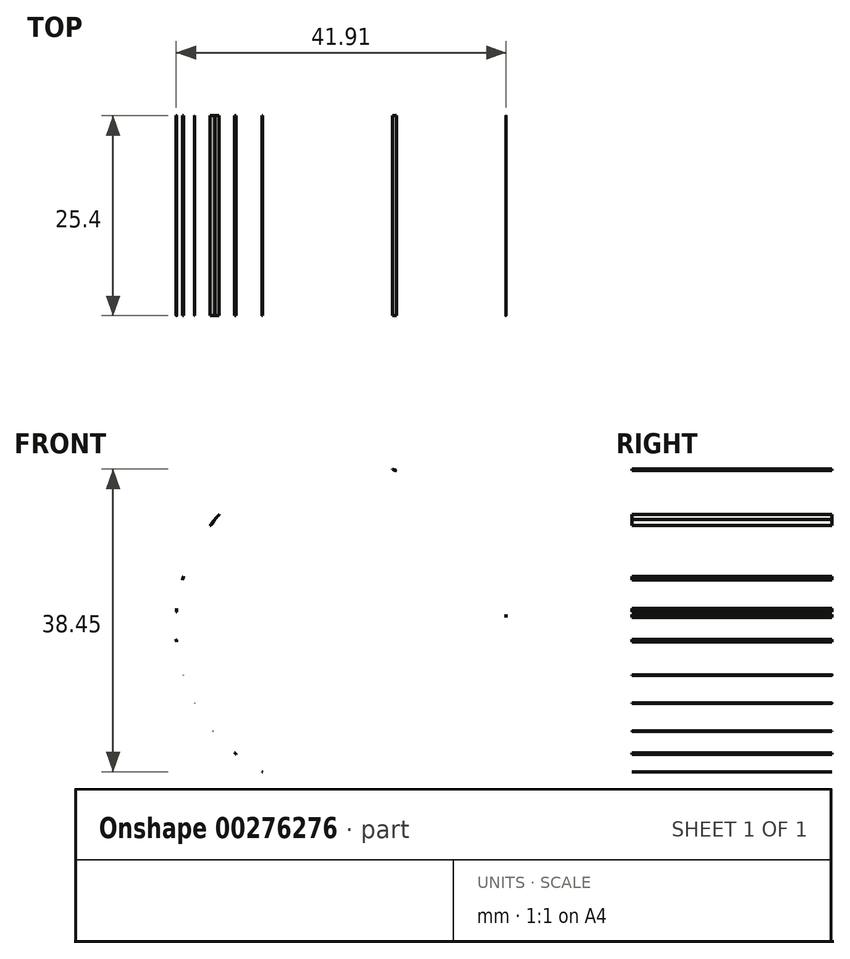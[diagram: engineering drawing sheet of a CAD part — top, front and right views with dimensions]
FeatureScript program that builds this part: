
annotation { "Feature Type Name" : "Feature", "Feature Type Description" : "" }
export const myFeature = defineFeature(function(context is Context, id is Id, definition is map)
    precondition{}
    {
        {
            var Q0;
            Q0=qCreatedBy(makeId("Front.planeOp"),FACE);
            var sketch = newSketch(context, id + "F0", { "sketchPlane" : qUnion([Q0])});
            skArc(sketch, "E0", {"start": v(-8.8, 19.07) * mm, "mid": v(-9.64, 18.66) * mm, "end": v(-10.46, 18.21) * mm});
            skFitSpline(sketch, "E1", {"points": [v(-18.48, 9.99) * mm, v(-18.56, 11.27) * mm, v(-19.16, 12.08) * mm, v(-19.57, 12.7) * mm, v(-19.03, 13.5) * mm, v(-18.35, 13.3) * mm, v(-16.64, 12.82) * mm, v(-16.01, 13.59) * mm, v(-15.5, 14.18) * mm], "startDerivative": vector(0.44, 9.8) * mm, "endDerivative": vector(5.2, 4.49) * mm});
            skFitSpline(sketch, "E2", {"points": [v(-15.5, 14.18) * mm, v(-15.5, 14.85) * mm, v(-16.13, 15.84) * mm, v(-16.63, 16.6) * mm, v(-16.17, 16.83) * mm, v(-15.5, 16.43) * mm, v(-13.9, 15.74) * mm], "startDerivative": vector(0.69, 4.6) * mm, "endDerivative": vector(7.86, -2.86) * mm});
            skFitSpline(sketch, "E3", {"points": [v(-12.52, 16.87) * mm, v(-12.57, 17.55) * mm, v(-12.93, 18.36) * mm, v(-13.16, 19.22) * mm, v(-12.39, 19.76) * mm, v(-11.67, 19.27) * mm, v(-10.46, 18.21) * mm], "startDerivative": vector(-0.05, 4.91) * mm, "endDerivative": vector(6.08, -4.97) * mm});
            skFitSpline(sketch, "E4", {"points": [v(-8.8, 19.07) * mm, v(-8.56, 19.72) * mm, v(-8.78, 20.75) * mm, v(-8.92, 21.56) * mm, v(-8.51, 21.74) * mm, v(-7.93, 21.2) * mm, v(-7.34, 20.21) * mm, v(-6.6, 19.94) * mm], "startDerivative": vector(2.55, 4.58) * mm, "endDerivative": vector(5.7, -1.1) * mm});
            skFitSpline(sketch, "E5", {"points": [v(-5.01, 20.4) * mm, v(-4.77, 21.2) * mm, v(-4.73, 21.88) * mm, v(-4.6, 22.92) * mm, v(-3.7, 23.1) * mm, v(-3.42, 22.2) * mm, v(-2.33, 20.87) * mm], "startDerivative": vector(1.77, 5.6) * mm, "endDerivative": vector(6.46, -5.84) * mm});
            skFitSpline(sketch, "E6", {"points": [v(-0.77, 20.99) * mm, v(-0.27, 21.56) * mm, v(0, 22.61) * mm, v(0.23, 23.47) * mm, v(0.59, 23.45) * mm, v(0.85, 22.57) * mm, v(1.04, 21.66) * mm, v(1.5, 20.95) * mm], "startDerivative": vector(3.99, 3.8) * mm, "endDerivative": vector(3.57, -4.76) * mm});
            skFitSpline(sketch, "E7", {"points": [v(3.08, 20.78) * mm, v(3.52, 21.18) * mm, v(3.93, 21.73) * mm, v(4.22, 22.26) * mm, v(4.62, 23.02) * mm, v(5.46, 22.78) * mm, v(5.5, 21.87) * mm, v(5.53, 21.09) * mm, v(6.05, 20.37) * mm, v(7.04, 19.79) * mm, v(8.15, 20.44) * mm, v(8.68, 20.94) * mm, v(9.42, 21.7) * mm, v(9.8, 21.35) * mm, v(9.56, 20.54) * mm, v(9.52, 19.44) * mm, v(9.88, 18.53) * mm], "startDerivative": vector(8.69, 7.41) * mm, "endDerivative": vector(6.45, -13.14) * mm});
            skFitSpline(sketch, "E8", {"points": [v(10.72, 18.06) * mm, v(11.3, 18.22) * mm, v(12.36, 19.01) * mm, v(13.1, 19.6) * mm, v(13.88, 19.01) * mm, v(13.6, 18.22) * mm, v(13.31, 17.2) * mm, v(13.3, 16.25) * mm], "startDerivative": vector(4.75, 0.92) * mm, "endDerivative": vector(0.2, -6.55) * mm});
            skFitSpline(sketch, "E9", {"points": [v(14.26, 15.42) * mm, v(15.3, 15.48) * mm, v(16.2, 16.12) * mm, v(16.96, 16.63) * mm, v(17.35, 16.17) * mm, v(16.87, 15.53) * mm, v(16.3, 14.6) * mm, v(16.09, 13.5) * mm], "startDerivative": vector(7.23, -0.38) * mm, "endDerivative": vector(-0.83, -7.21) * mm});
            skFitSpline(sketch, "E10", {"points": [v(16.56, 12.91) * mm, v(17.1, 12.56) * mm, v(18.82, 12.88) * mm, v(19.74, 13.2) * mm, v(20.3, 12.5) * mm, v(19.76, 11.75) * mm, v(18.6, 10.15) * mm, v(18.67, 9.63) * mm], "startDerivative": vector(3.76, -3.9) * mm, "endDerivative": vector(1.69, -4.44) * mm});
            skFitSpline(sketch, "E11", {"points": [v(18.95, 9.05) * mm, v(19.92, 8.58) * mm, v(21.1, 8.78) * mm, v(22.08, 8.92) * mm, v(22.38, 8.14) * mm, v(21.8, 7.7) * mm, v(20.63, 6.59) * mm, v(20.23, 5.64) * mm], "startDerivative": vector(6.45, -4.25) * mm, "endDerivative": vector(-1.89, -6.56) * mm});
            skFitSpline(sketch, "E12", {"points": [v(20.3, 5.37) * mm, v(21.17, 4.56) * mm, v(23.36, 4.7) * mm, v(23.76, 3.72) * mm, v(22.75, 3.25) * mm, v(21.4, 2.37) * mm, v(20.97, 1.15) * mm, v(22, 0.45) * mm, v(23.46, 0) * mm, v(24.1, 0) * mm, v(24.14, -0.87) * mm, v(23.2, -1) * mm, v(21.67, -1.51) * mm, v(20.88, -2.28) * mm], "startDerivative": vector(8.37, -14.78) * mm, "endDerivative": vector(-9.5, -11.08) * mm});
            skFitSpline(sketch, "E13", {"points": [v(20.72, -3.41) * mm, v(22.5, -4.36) * mm, v(23.64, -4.8) * mm, v(23.45, -5.82) * mm, v(22.5, -5.76) * mm, v(20.88, -6.14) * mm, v(19.9, -6.7) * mm], "startDerivative": vector(8.48, -5.65) * mm, "endDerivative": vector(-5.76, -3.62) * mm});
            skFitSpline(sketch, "E14", {"points": [v(19.7, -7.27) * mm, v(20.3, -8.37) * mm, v(21.54, -9.07) * mm, v(20.88, -10.22) * mm, v(19.5, -10.03) * mm, v(18.13, -10.6) * mm], "startDerivative": vector(1.79, -6.7) * mm, "endDerivative": vector(-6.48, -4.32) * mm});
            skFitSpline(sketch, "E15", {"points": [v(18.13, -10.6) * mm, v(18.67, -11.94) * mm, v(19.7, -12.68) * mm, v(20.3, -13.35) * mm, v(19.66, -14.2) * mm, v(18.67, -13.8) * mm, v(17.05, -13.67) * mm, v(16.18, -13.4) * mm], "startDerivative": vector(2.4, -9.38) * mm, "endDerivative": vector(-6.14, 2.82) * mm});
            skFitSpline(sketch, "E16", {"points": [v(15.83, -13.8) * mm, v(15.83, -15.02) * mm, v(16.73, -16.42) * mm, v(17.05, -16.96) * mm, v(16.64, -17.5) * mm, v(16.1, -17.14) * mm, v(15.1, -16.5) * mm, v(13.8, -16.37) * mm, v(12.91, -16.56) * mm], "startDerivative": vector(-1.34, -8.58) * mm, "endDerivative": vector(-7.06, -1.86) * mm});
            skFitSpline(sketch, "E17", {"points": [v(13.2, -16.5) * mm, v(13.2, -17.63) * mm, v(13.58, -19.48) * mm, v(13.67, -20.07) * mm, v(13.2, -20.6) * mm, v(12.63, -20.3) * mm, v(11.1, -19.3) * mm, v(10.06, -19.57) * mm, v(9.48, -20.38) * mm, v(9.57, -21.64) * mm, v(9.61, -22.36) * mm, v(8.76, -22.86) * mm, v(7.85, -21.55) * mm, v(6.55, -20.92) * mm, v(5.65, -21.42) * mm, v(5.24, -22.18) * mm, v(5.24, -23.85) * mm, v(4.11, -24.03) * mm, v(3.53, -23.09) * mm, v(3.03, -22.14) * mm, v(2.22, -21.87) * mm, v(1.5, -22.14) * mm, v(0.87, -22.72) * mm, v(0.42, -24.35) * mm, v(-0.75, -24.26) * mm, v(-0.89, -23.5) * mm, v(-1.43, -22.14) * mm, v(-2.42, -21.87) * mm, v(-3.55, -22.63) * mm, v(-4.22, -23.76) * mm, v(-5.48, -23.67) * mm, v(-5.4, -22.18) * mm, v(-5.8, -21.1) * mm, v(-5.93, -20.15) * mm], "startDerivative": vector(-2.35, -33.34) * mm, "endDerivative": vector(-0.5, 35.14) * mm});
            skLineSegment(sketch, "E18", {"start": v(-1.92, -21.87) * mm, "end": v(-1.92, -20.91) * mm});
            skLineSegment(sketch, "E19", {"start": v(2.13, -20.9) * mm, "end": v(2.22, -21.87) * mm});
            skLineSegment(sketch, "E20", {"start": v(6.55, -20.92) * mm, "end": v(6.12, -20.1) * mm});
            skLineSegment(sketch, "E21", {"start": v(10.06, -19.57) * mm, "end": v(10.06, -18.43) * mm});
            skFitSpline(sketch, "E22", {"points": [v(-5.93, -20.48) * mm, v(-7.16, -20.48) * mm, v(-8.31, -21.73) * mm, v(-9, -22.45) * mm, v(-9.84, -22.07) * mm, v(-9.46, -20.48) * mm, v(-9.84, -19.18) * mm, v(-9.98, -18.48) * mm, v(-11.12, -18.8) * mm, v(-12.44, -19.73) * mm, v(-13.16, -20.48) * mm, v(-13.97, -19.73) * mm, v(-13.59, -18.88) * mm, v(-13.29, -17.27) * mm, v(-13.32, -16.24) * mm, v(-14.48, -15.95) * mm, v(-15.93, -16.59) * mm, v(-16.78, -17.27) * mm, v(-17.33, -16.71) * mm, v(-16.73, -15.73) * mm, v(-16.14, -14.37) * mm, v(-16.24, -13.31) * mm, v(-17.37, -13.01) * mm, v(-18.73, -13.35) * mm, v(-19.84, -13.74) * mm, v(-20.3, -12.97) * mm, v(-19.67, -12.2) * mm, v(-18.73, -10.67) * mm, v(-18.58, -9.79) * mm, v(-19.54, -9.23) * mm, v(-21.2, -9.36) * mm, v(-22, -9.48) * mm, v(-22.3, -8.72) * mm, v(-21.45, -8.16) * mm, v(-20.3, -7.23) * mm, v(-20.08, -6.16) * mm, v(-20.99, -5.37) * mm, v(-22.49, -5.04) * mm, v(-23.3, -5.15) * mm, v(-23.45, -4.03) * mm, v(-22.6, -3.54) * mm, v(-20.9, -1.99) * mm, v(-21.74, -0.92) * mm, v(-23.35, -0.49) * mm, v(-23.88, 0) * mm, v(-23.61, 0.48) * mm, v(-22.49, 0.69) * mm, v(-20.93, 1.8) * mm, v(-21.3, 3.1) * mm, v(-22.43, 3.85) * mm, v(-23.19, 4.39) * mm, v(-22.86, 5.2) * mm, v(-21.95, 5.2) * mm, v(-20.15, 5.91) * mm, v(-20.24, 7.12) * mm, v(-21.2, 8.3) * mm, v(-21.95, 8.83) * mm, v(-21.36, 9.58) * mm, v(-20.61, 9.48) * mm, v(-18.75, 9.46) * mm], "startDerivative": vector(-73.72, 15.48) * mm, "endDerivative": vector(99.26, 5.76) * mm});
            skArc(sketch, "E23.trimOffspring", {"start": v(-5.01, 20.4) * mm, "mid": v(-5.81, 20.18) * mm, "end": v(-6.6, 19.94) * mm});
            skArc(sketch, "E24.trimOffspring", {"start": v(-0.77, 20.99) * mm, "mid": v(-1.55, 20.95) * mm, "end": v(-2.33, 20.87) * mm});
            skArc(sketch, "E25.trimOffspring", {"start": v(3.08, 20.78) * mm, "mid": v(2.29, 20.88) * mm, "end": v(1.5, 20.95) * mm});
            skArc(sketch, "E26.trimOffspring", {"start": v(7.04, 19.79) * mm, "mid": v(6.77, 19.88) * mm, "end": v(6.51, 19.97) * mm});
            skArc(sketch, "E27.trimOffspring", {"start": v(10.72, 18.06) * mm, "mid": v(10.3, 18.3) * mm, "end": v(9.88, 18.53) * mm});
            skArc(sketch, "E28.trimOffspring", {"start": v(14.26, 15.42) * mm, "mid": v(13.79, 15.85) * mm, "end": v(13.3, 16.25) * mm});
            skArc(sketch, "E29.trimOffspring", {"start": v(16.56, 12.91) * mm, "mid": v(16.33, 13.2) * mm, "end": v(16.09, 13.5) * mm});
            skArc(sketch, "E30.trimOffspring", {"start": v(18.95, 9.05) * mm, "mid": v(18.81, 9.34) * mm, "end": v(18.67, 9.63) * mm});
            skArc(sketch, "E31.trimOffspring", {"start": v(20.3, 5.37) * mm, "mid": v(20.27, 5.5) * mm, "end": v(20.23, 5.64) * mm});
            skArc(sketch, "E32.trimOffspring", {"start": v(20.97, 1.15) * mm, "mid": v(20.96, 1.32) * mm, "end": v(20.95, 1.49) * mm});
            skArc(sketch, "E33.trimOffspring", {"start": v(20.72, -3.41) * mm, "mid": v(20.8, -2.85) * mm, "end": v(20.88, -2.28) * mm});
            skArc(sketch, "E34.trimOffspring", {"start": v(19.7, -7.27) * mm, "mid": v(19.8, -6.99) * mm, "end": v(19.9, -6.7) * mm});
            skArc(sketch, "E35.trimOffspring", {"start": v(15.83, -13.8) * mm, "mid": v(16, -13.6) * mm, "end": v(16.18, -13.4) * mm});
            skArc(sketch, "E36.trimOffspring", {"start": v(-10.02, -18.46) * mm, "mid": v(-10, -18.47) * mm, "end": v(-9.98, -18.48) * mm});
            skArc(sketch, "E37.trimOffspring", {"start": v(-13.5, -16.1) * mm, "mid": v(-13.4, -16.17) * mm, "end": v(-13.32, -16.24) * mm});
            skArc(sketch, "E38.trimOffspring", {"start": v(-16.24, -13.31) * mm, "mid": v(-16.23, -13.33) * mm, "end": v(-16.22, -13.34) * mm});
            skArc(sketch, "E39.trimOffspring", {"start": v(-18.6, -9.74) * mm, "mid": v(-18.6, -9.77) * mm, "end": v(-18.58, -9.79) * mm});
            skArc(sketch, "E40.trimOffspring", {"start": v(-20.08, -6.16) * mm, "mid": v(-20.07, -6.19) * mm, "end": v(-20.06, -6.21) * mm});
            skArc(sketch, "E41.trimOffspring", {"start": v(-20.94, -1.66) * mm, "mid": v(-20.92, -1.82) * mm, "end": v(-20.9, -1.99) * mm});
            skArc(sketch, "E42.trimOffspring", {"start": v(-20.88, 2.25) * mm, "mid": v(-20.9, 2.03) * mm, "end": v(-20.93, 1.8) * mm});
            skArc(sketch, "E43.trimOffspring", {"start": v(-20.02, 6.35) * mm, "mid": v(-20.09, 6.13) * mm, "end": v(-20.15, 5.91) * mm});
            skArc(sketch, "E44.trimOffspring", {"start": v(-18.48, 9.99) * mm, "mid": v(-18.62, 9.72) * mm, "end": v(-18.75, 9.46) * mm});
            skArc(sketch, "E45.trimOffspring", {"start": v(-15.5, 14.18) * mm, "mid": v(-16.08, 13.51) * mm, "end": v(-16.64, 12.82) * mm});
            skArc(sketch, "E46.trimOffspring", {"start": v(-12.52, 16.87) * mm, "mid": v(-13.22, 16.32) * mm, "end": v(-13.9, 15.74) * mm});
            skSolve(sketch);
        }
        {
            var Q0;
            Q0 = qSketchRegion(id + "F0", true);
            extrude(context, id + "F1", {"entities" : qUnion([Q0]), "depth" : 25.4 * mm});
        }
    });
